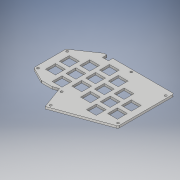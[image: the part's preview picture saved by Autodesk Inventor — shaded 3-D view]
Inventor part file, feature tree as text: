
AUTODESK INVENTOR PART (.ipt)
format: ipt  version: 2017 (Build 210142000, 142)  size: 252,416 bytes
history: native  units: in
note: dims shown in document units (in); Inventor stores cm internally (conversion verified against a paired STEP export)
features: extrude x4, other x3, pattern_linear x2, sketch x2
ambient origin geometry x8: Origin, YZ Plane, XZ Plane, XY Plane, X Axis, Y Axis, Z Axis, Center Point
bodies: Body1 (feature_tree)
feature tree (11):
  other  "k2_base.ipt"
  extrude  "Extrusion5"  Depth=0.3937in TaperAngle=0.0deg
  extrude  "Extrusion6"  Depth=0.5315in
  extrude  "Extrusion7"  TaperAngle=0.0deg  [1 undecoded]
  pattern_linear  "Rectangular Pattern7"  Spacing1=0.5315in  [1 undecoded]
  pattern_linear  "Rectangular Pattern8"  Spacing1=0.5315in  [1 undecoded]
  extrude  "Extrusion8"  Depth=0.3937in TaperAngle=0.0deg
  sketch  "Sketch6"  dims[d73=0.5315in d74=0.5315in d75=0.5315in d76=0.5315in d77=0.5315in d78=0.5315in d79=0.5315in d80=0.5315in d81=0.2165in d82=0.2165in d83=0.2165in d84=0.315in d85=0.2756in d86=0.4331in d92=0.3937in d93=0.0in]
  other  "Solid5::k2_base.ipt"
  other  "TaggingFeature2"
  sketch  "Sketch10"  dims[d97=0.5315in d98=0.5315in d101=0.0in d102=0.0in d106=0.5315in d107=0.5315in d110=0.3937in d111=0.0in d115=0.3937in d116=1.0827in d119=0.5512in d120=0.2165in d121=0.3937in d122=0.3937in d123=0.2165in d124=1.1811in d126=0.748in d127=0.7874in d129=0.748in d130=1.2992in d131=0.315in d132=0.3937in d133=0.0in]
note: 3 required parameter values undecoded (feature->parameter linkage not recoverable at this tier; creation-order binding heuristic only, values carry confidence <= 0.55)
